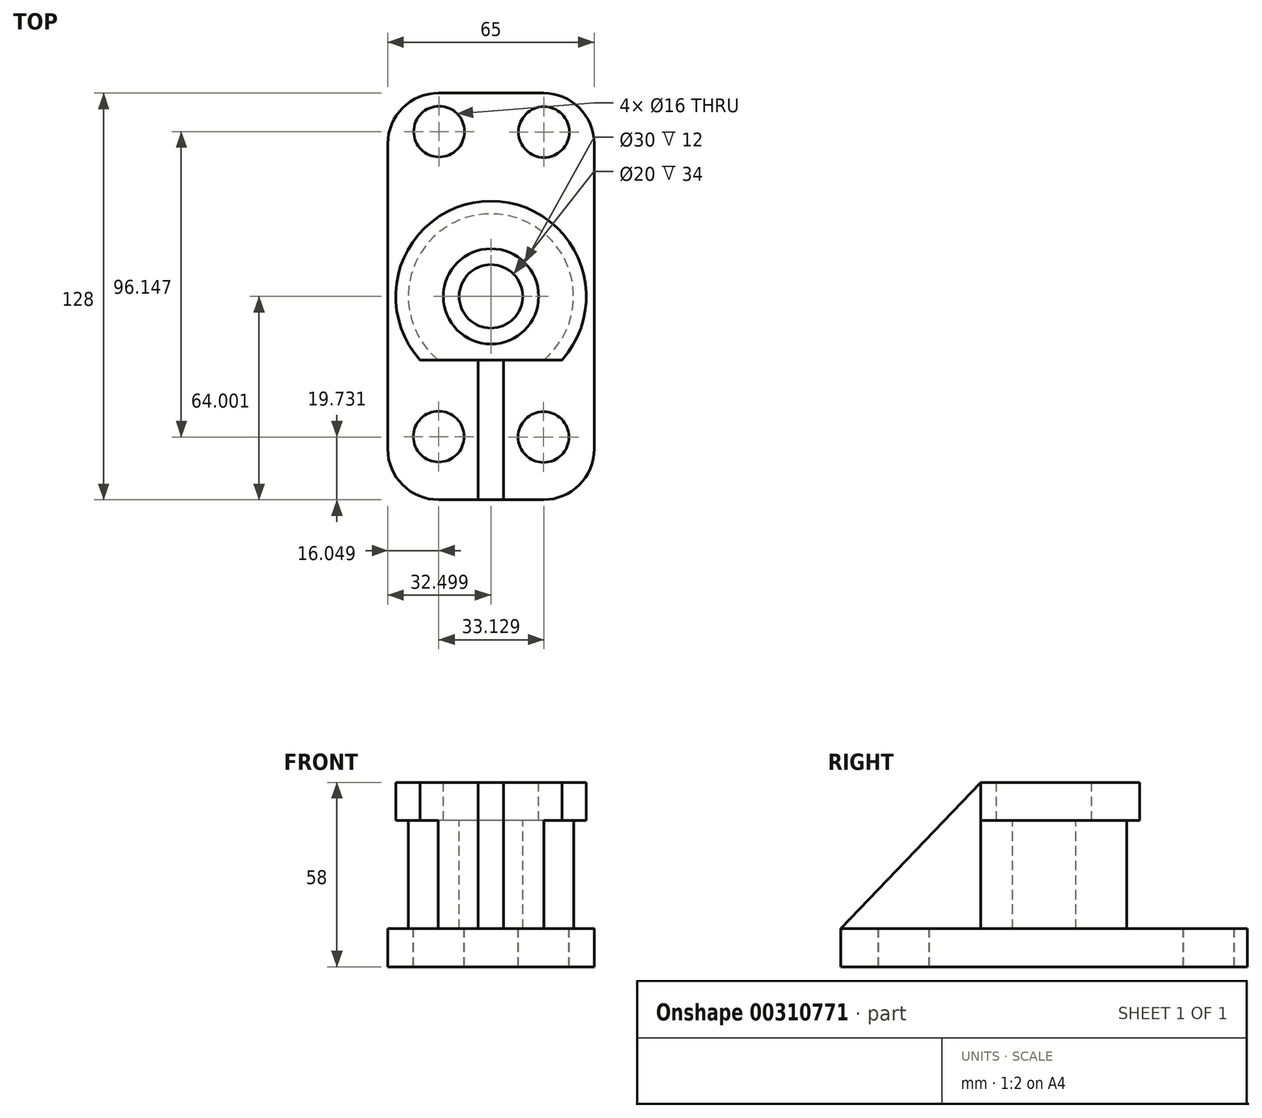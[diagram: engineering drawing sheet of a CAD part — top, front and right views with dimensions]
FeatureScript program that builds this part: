
annotation { "Feature Type Name" : "Feature", "Feature Type Description" : "" }
export const myFeature = defineFeature(function(context is Context, id is Id, definition is map)
    precondition{}
    {
        {
            var Q0;
            Q0=qCreatedBy(makeId("Top.planeOp"),FACE);
            var sketch = newSketch(context, id + "F0", { "sketchPlane" : qUnion([Q0])});
            skLineSegment(sketch, "E0", {"start": v(-44.48, 67.15) * mm, "end": v(-44.48, -60.85) * mm});
            skLineSegment(sketch, "E1", {"start": v(-44.48, -60.85) * mm, "end": v(20.52, -60.85) * mm});
            skLineSegment(sketch, "E2", {"start": v(20.52, 67.15) * mm, "end": v(20.52, -60.85) * mm});
            skLineSegment(sketch, "E3", {"start": v(-44.48, 67.15) * mm, "end": v(20.52, 67.15) * mm});
            skSolve(sketch);
        }
        {
            var Q0;
            Q0=makeQuery(id+"F0.imprint","IMPRINT",FACE,{"disambiguationData":[TD([[makeQuery(id+"F0.imprint","IMPRINT",EDGE,{"derivedFrom":sQuery(id+"F0.wireOp",EDGE,"E0")}),1.0]])]});
            extrude(context, id + "F1", {"entities" : qUnion([Q0]), "depth" : 12 * mm});
        }
        {
            var Q0;
            Q0=makeQuery(id+"F1.opExtrude","SWEPT_EDGE",EDGE,{"disambiguationData":[OSD([sQuery(id+"F0.wireOp",EDGE,"E1"),sQuery(id+"F0.wireOp",EDGE,"E2")])]});
            var Q1;
            Q1=makeQuery(id+"F1.opExtrude","SWEPT_EDGE",EDGE,{"disambiguationData":[OSD([sQuery(id+"F0.wireOp",EDGE,"E2"),sQuery(id+"F0.wireOp",EDGE,"E3")])]});
            var Q2;
            Q2=makeQuery(id+"F1.opExtrude","SWEPT_EDGE",EDGE,{"disambiguationData":[OSD([sQuery(id+"F0.wireOp",EDGE,"E0"),sQuery(id+"F0.wireOp",EDGE,"E1")])]});
            var Q3;
            Q3=makeQuery(id+"F1.opExtrude","SWEPT_EDGE",EDGE,{"disambiguationData":[OSD([sQuery(id+"F0.wireOp",EDGE,"E0"),sQuery(id+"F0.wireOp",EDGE,"E3")])]});
            fillet(context, id + "F2", {"entities" : qUnion([Q0, Q1, Q2, Q3]), "radius" : 16 * mm, "tangentPropagation" : true, "allowEdgeOverflow" : false});
        }
        {
            var Q0;
            Q0=makeQuery(id+"F1.opExtrude","CAP_FACE",FACE,{"disambiguationData":[OSD([sQuery(id+"F0.wireOp",EDGE,"E0"),sQuery(id+"F0.wireOp",EDGE,"E1"),sQuery(id+"F0.wireOp",EDGE,"E2"),sQuery(id+"F0.wireOp",EDGE,"E3")])],"isStart":false});
            var sketch = newSketch(context, id + "F3", { "sketchPlane" : qUnion([Q0])});
            skCircle(sketch, "E4", {"center": v(4.57, -41.12) * mm, "radius": 8 * mm});
            skCircle(sketch, "E5", {"center": v(-28.43, -40.97) * mm, "radius": 8 * mm});
            skCircle(sketch, "E6", {"center": v(-28.3, 55.03) * mm, "radius": 8 * mm});
            skCircle(sketch, "E7", {"center": v(4.7, 54.88) * mm, "radius": 8 * mm});
            skSolve(sketch);
        }
        {
            var Q0;
            Q0=makeQuery(id+"F3.imprint","IMPRINT",FACE,{"disambiguationData":[TD([[makeQuery(id+"F3.imprint","IMPRINT",EDGE,{"derivedFrom":sQuery(id+"F3.wireOp",EDGE,"E4")}),1.0]])]});
            var Q1;
            Q1=makeQuery(id+"F3.imprint","IMPRINT",FACE,{"disambiguationData":[TD([[makeQuery(id+"F3.imprint","IMPRINT",EDGE,{"derivedFrom":sQuery(id+"F3.wireOp",EDGE,"E5")}),1.0]])]});
            var Q2;
            Q2=makeQuery(id+"F3.imprint","IMPRINT",FACE,{"disambiguationData":[TD([[makeQuery(id+"F3.imprint","IMPRINT",EDGE,{"derivedFrom":sQuery(id+"F3.wireOp",EDGE,"E7")}),1.0]])]});
            var Q3;
            Q3=makeQuery(id+"F3.imprint","IMPRINT",FACE,{"disambiguationData":[TD([[makeQuery(id+"F3.imprint","IMPRINT",EDGE,{"derivedFrom":sQuery(id+"F3.wireOp",EDGE,"E6")}),1.0]])]});
            extrude(context, id + "F4", {"entities" : qUnion([Q0, Q1, Q2, Q3]), "operationType" : NewBodyOperationType.REMOVE, "oppositeDirection" : true, "depth" : 25 * mm});
        }
        {
            var Q0;
            Q0=makeQuery(id+"F1.opExtrude","CAP_FACE",FACE,{"disambiguationData":[OSD([sQuery(id+"F0.wireOp",EDGE,"E0"),sQuery(id+"F0.wireOp",EDGE,"E1"),sQuery(id+"F0.wireOp",EDGE,"E2"),sQuery(id+"F0.wireOp",EDGE,"E3")])],"isStart":false});
            var sketch = newSketch(context, id + "F5", { "sketchPlane" : qUnion([Q0])});
            skLineSegment(sketch, "E8", {"start": v(-11.98, -60.85) * mm, "end": v(-11.98, 67.15) * mm});
            skLineSegment(sketch, "E9", {"start": v(-44.48, 3.15) * mm, "end": v(20.52, 3.15) * mm});
            skCircle(sketch, "E10", {"center": v(-11.98, 3.15) * mm, "radius": 26 * mm});
            skLineSegment(sketch, "E11", {"start": v(-28.6, -16.85) * mm, "end": v(4.63, -16.85) * mm});
            skSolve(sketch);
        }
        {
            var Q0;
            {var subQ0=sQuery(id+"F5.wireOp",EDGE,"E11");var subQ1=sQuery(id+"F5.wireOp",EDGE,"E8");var subQ2=makeQuery(id+"F5.imprint","INTERSECT",VERTEX,{"derivedFrom":[subQ1,subQ0]});Q0=makeQuery(id+"F5.imprint","IMPRINT",FACE,{"disambiguationData":[TD([[makeQuery(id+"F5.imprint","IMPRINT",EDGE,{"disambiguationData":[TD([[subQ2,-1.0]])],"derivedFrom":subQ1}),-1.0]])]});}
            var Q1;
            {var subQ0=sQuery(id+"F5.wireOp",EDGE,"E9");var subQ1=sQuery(id+"F5.wireOp",EDGE,"E8");var subQ2=makeQuery(id+"F5.imprint","INTERSECT",VERTEX,{"derivedFrom":[subQ1,subQ0]});Q1=makeQuery(id+"F5.imprint","IMPRINT",FACE,{"disambiguationData":[TD([[makeQuery(id+"F5.imprint","IMPRINT",EDGE,{"disambiguationData":[TD([[subQ2,-1.0]])],"derivedFrom":subQ1}),-1.0]])]});}
            var Q2;
            {var subQ0=sQuery(id+"F5.wireOp",EDGE,"E9");var subQ1=sQuery(id+"F5.wireOp",EDGE,"E8");var subQ2=makeQuery(id+"F5.imprint","INTERSECT",VERTEX,{"derivedFrom":[subQ1,subQ0]});Q2=makeQuery(id+"F5.imprint","IMPRINT",FACE,{"disambiguationData":[TD([[makeQuery(id+"F5.imprint","IMPRINT",EDGE,{"disambiguationData":[TD([[subQ2,-1.0]])],"derivedFrom":subQ1}),1.0]])]});}
            var Q3;
            {var subQ0=sQuery(id+"F5.wireOp",EDGE,"E11");var subQ1=sQuery(id+"F5.wireOp",EDGE,"E8");var subQ2=makeQuery(id+"F5.imprint","INTERSECT",VERTEX,{"derivedFrom":[subQ1,subQ0]});Q3=makeQuery(id+"F5.imprint","IMPRINT",FACE,{"disambiguationData":[TD([[makeQuery(id+"F5.imprint","IMPRINT",EDGE,{"disambiguationData":[TD([[subQ2,-1.0]])],"derivedFrom":subQ1}),1.0]])]});}
            extrude(context, id + "F6", {"entities" : qUnion([Q0, Q1, Q2, Q3]), "operationType" : NewBodyOperationType.ADD, "depth" : 46 * mm});
        }
        {
            var Q0;
            Q0=makeQuery(id+"F1.opExtrude","CAP_FACE",FACE,{"disambiguationData":[OSD([sQuery(id+"F0.wireOp",EDGE,"E0"),sQuery(id+"F0.wireOp",EDGE,"E1"),sQuery(id+"F0.wireOp",EDGE,"E2"),sQuery(id+"F0.wireOp",EDGE,"E3")])],"isStart":false});
            var sketch = newSketch(context, id + "F7", { "sketchPlane" : qUnion([Q0])});
            skLineSegment(sketch, "E12", {"start": v(-15.98, -60.85) * mm, "end": v(-15.98, -16.85) * mm});
            skLineSegment(sketch, "E13", {"start": v(-7.98, -60.85) * mm, "end": v(-7.98, -16.85) * mm});
            skSolve(sketch);
        }
        {
            var Q0;
            {var subQ0=sQuery(id+"F5.wireOp",EDGE,"E11");Q0=makeQuery(id+"FNBuvGpGdWqQCqh_1.boolean.opBoolean","MERGE",FACE,{"derivedFrom":[makeQuery(id+"F6.opExtrude","CAP_FACE",FACE,{"disambiguationData":[OSD([sQuery(id+"F5.wireOp",EDGE,"E10"),subQ0])],"isStart":false}),makeQuery(id+"FNBuvGpGdWqQCqh_1.opExtrude","CAP_FACE",FACE,{"disambiguationData":[OSD([sQuery(id+"F0.wireOp",EDGE,"E1"),subQ0,sQuery(id+"F7.wireOp",EDGE,"E12"),sQuery(id+"F7.wireOp",EDGE,"E13")])],"isStart":false})]});}
            var sketch = newSketch(context, id + "F8", { "sketchPlane" : qUnion([Q0])});
            skCircle(sketch, "E14", {"center": v(-11.98, 3.15) * mm, "radius": 15 * mm});
            skCircle(sketch, "E15", {"center": v(-11.98, 3.15) * mm, "radius": 10 * mm});
            skSolve(sketch);
        }
        {
            var Q0;
            Q0=makeQuery(id+"F8.imprint","IMPRINT",FACE,{"disambiguationData":[TD([[makeQuery(id+"F8.imprint","IMPRINT",EDGE,{"derivedFrom":sQuery(id+"F8.wireOp",EDGE,"E14")}),1.0]])]});
            extrude(context, id + "F9", {"entities" : qUnion([Q0]), "operationType" : NewBodyOperationType.REMOVE, "oppositeDirection" : true, "depth" : 12 * mm});
        }
        {
            var Q0;
            {var subQ0=sQuery(id+"F5.wireOp",EDGE,"E11");Q0=makeQuery(id+"F9.boolean.opBoolean","SPLIT",FACE,{"disambiguationData":[TD([makeQuery(id+"F9.opExtrude","SWEPT_FACE",FACE,{"disambiguationData":[OSD([sQuery(id+"F8.wireOp",EDGE,"E15")])]})])],"derivedFrom":makeQuery(id+"FNBuvGpGdWqQCqh_1.boolean.opBoolean","MERGE",FACE,{"derivedFrom":[makeQuery(id+"F6.opExtrude","CAP_FACE",FACE,{"disambiguationData":[OSD([sQuery(id+"F5.wireOp",EDGE,"E10"),subQ0])],"isStart":false}),makeQuery(id+"FNBuvGpGdWqQCqh_1.opExtrude","CAP_FACE",FACE,{"disambiguationData":[OSD([sQuery(id+"F0.wireOp",EDGE,"E1"),subQ0,sQuery(id+"F7.wireOp",EDGE,"E12"),sQuery(id+"F7.wireOp",EDGE,"E13")])],"isStart":false})]})});}
            extrude(context, id + "F10", {"entities" : qUnion([Q0]), "operationType" : NewBodyOperationType.REMOVE, "oppositeDirection" : true, "depth" : 46 * mm});
        }
        {
            var Q0;
            {var subQ0=sQuery(id+"F7.wireOp",EDGE,"E13");var subQ1=sQuery(id+"F7.wireOp",EDGE,"E12");var subQ2=sQuery(id+"F5.wireOp",EDGE,"E11");var subQ3=sQuery(id+"F5.wireOp",EDGE,"E10");Q0=makeQuery(id+"F9.boolean.opBoolean","SPLIT",FACE,{"disambiguationData":[TD([makeQuery(id+"F6.opExtrude","SWEPT_FACE",FACE,{"disambiguationData":[OSD([subQ3])]})])],"derivedFrom":makeQuery(id+"FNBuvGpGdWqQCqh_1.boolean.opBoolean","MERGE",FACE,{"derivedFrom":[makeQuery(id+"F6.opExtrude","CAP_FACE",FACE,{"disambiguationData":[OSD([subQ3,subQ2])],"isStart":false}),makeQuery(id+"FNBuvGpGdWqQCqh_1.opExtrude","CAP_FACE",FACE,{"disambiguationData":[OSD([sQuery(id+"F0.wireOp",EDGE,"E1"),subQ2,subQ1,subQ0])],"isStart":false})]})});}
            var sketch = newSketch(context, id + "F11", { "sketchPlane" : qUnion([Q0])});
            skArc(sketch, "E16.0", {"start": v(4.63, -16.85) * mm, "mid": v(-11.98, 29.15) * mm, "end": v(-28.6, -16.85) * mm});
            skSolve(sketch);
        }
        {
            var Q0;
            Q0 = qSketchRegion(id + "F11", true);
            var Q1;
            Q1=makeQuery(id+"F11.imprint","IMPRINT",FACE,{"disambiguationData":[TD([[makeQuery(id+"F11.imprint","IMPRINT",EDGE,{"derivedFrom":sQuery(id+"F11.wireOp",EDGE,"E16.0")}),1.0]])]});
            extrude(context, id + "F12", {"entities" : qUnion([Q0, Q1]), "operationType" : NewBodyOperationType.ADD, "oppositeDirection" : true, "depth" : 25 * mm});
        }
        {
            var Q0;
            {var subQ0=sQuery(id+"F5.wireOp",EDGE,"E10");var subQ1=sQuery(id+"F5.wireOp",EDGE,"E11");Q0=makeQuery(id+"F9.boolean.opBoolean","SPLIT",FACE,{"disambiguationData":[TD([makeQuery(id+"F6.opExtrude","SWEPT_FACE",FACE,{"disambiguationData":[OSD([subQ0])]})])],"derivedFrom":makeQuery(id+"F6.opExtrude","CAP_FACE",FACE,{"disambiguationData":[OSD([subQ0,subQ1])],"isStart":false})});}
            var sketch = newSketch(context, id + "F13", { "sketchPlane" : qUnion([Q0])});
            skArc(sketch, "E17.0.0", {"start": v(4.63, -16.85) * mm, "mid": v(-11.98, 29.15) * mm, "end": v(-28.6, -16.85) * mm});
            skLineSegment(sketch, "E17.0.1", {"start": v(-28.6, -16.85) * mm, "end": v(4.63, -16.85) * mm});
            skCircle(sketch, "E18", {"center": v(-11.98, 3.15) * mm, "radius": 30 * mm});
            skSolve(sketch);
        }
        {
            var Q0;
            Q0 = qSketchRegion(id + "F13", true);
            extrude(context, id + "F14", {"entities" : qUnion([Q0]), "operationType" : NewBodyOperationType.ADD, "oppositeDirection" : true, "depth" : 12 * mm});
        }
        {
            var Q0;
            {var subQ0=sQuery(id+"F5.wireOp",EDGE,"E10");var subQ1=sQuery(id+"F5.wireOp",EDGE,"E11");Q0=makeQuery(id+"F14.boolean.opBoolean","MERGE",FACE,{"derivedFrom":[makeQuery(id+"F9.boolean.opBoolean","SPLIT",FACE,{"disambiguationData":[TD([makeQuery(id+"F6.opExtrude","SWEPT_FACE",FACE,{"disambiguationData":[OSD([subQ0])]})])],"derivedFrom":makeQuery(id+"F6.opExtrude","CAP_FACE",FACE,{"disambiguationData":[OSD([subQ0,subQ1])],"isStart":false})}),makeQuery(id+"F14.opExtrude","CAP_FACE",FACE,{"disambiguationData":[OSD([sQuery(id+"F13.wireOp",EDGE,"E17.0.0"),sQuery(id+"F13.wireOp",EDGE,"E17.0.1"),sQuery(id+"F13.wireOp",EDGE,"E18")])],"isStart":true})]});}
            var sketch = newSketch(context, id + "F15", { "sketchPlane" : qUnion([Q0])});
            skLineSegment(sketch, "E19", {"start": v(-34.34, -16.85) * mm, "end": v(10.38, -16.85) * mm});
            skSolve(sketch);
        }
        {
            var Q0;
            {var subQ0=sQuery(id+"F15.wireOp",EDGE,"E19");Q0=makeQuery(id+"F15.imprint","IMPRINT",FACE,{"disambiguationData":[TD([[makeQuery(id+"F15.imprint","IMPRINT",EDGE,{"derivedFrom":subQ0}),-1.0]])]});}
            extrude(context, id + "F16", {"entities" : qUnion([Q0]), "operationType" : NewBodyOperationType.REMOVE, "oppositeDirection" : true, "depth" : 25 * mm});
        }
        {
            var Q0;
            Q0 = qSketchRegion(id + "F7", true);
            var Q1;
            {var subQ0=sQuery(id+"F7.wireOp",EDGE,"E12");Q1=makeQuery(id+"F7.imprint","IMPRINT",FACE,{"disambiguationData":[TD([[makeQuery(id+"F7.imprint","IMPRINT",EDGE,{"derivedFrom":subQ0}),-1.0]])]});}
            extrude(context, id + "F17", {"entities" : qUnion([Q0, Q1]), "operationType" : NewBodyOperationType.ADD, "depth" : 46 * mm});
        }
        {
            var Q0;
            Q0=makeQuery(id+"F17.opExtrude","SWEPT_FACE",FACE,{"disambiguationData":[OSD([sQuery(id+"F7.wireOp",EDGE,"E13")])]});
            var sketch = newSketch(context, id + "F18", { "sketchPlane" : qUnion([Q0])});
            skLineSegment(sketch, "E20", {"start": v(-16.85, 58) * mm, "end": v(-60.85, 12) * mm});
            skSolve(sketch);
        }
        {
            var Q0;
            Q0 = qSketchRegion(id + "F18", true);
            var Q1;
            Q1=makeQuery(id+"F18.imprint","IMPRINT",FACE,{"disambiguationData":[TD([[makeQuery(id+"F18.imprint","IMPRINT",EDGE,{"derivedFrom":sQuery(id+"F18.wireOp",EDGE,"E20")}),-1.0]])]});
            extrude(context, id + "F19", {"entities" : qUnion([Q0, Q1]), "operationType" : NewBodyOperationType.REMOVE, "oppositeDirection" : true, "depth" : 25 * mm});
        }
    });
